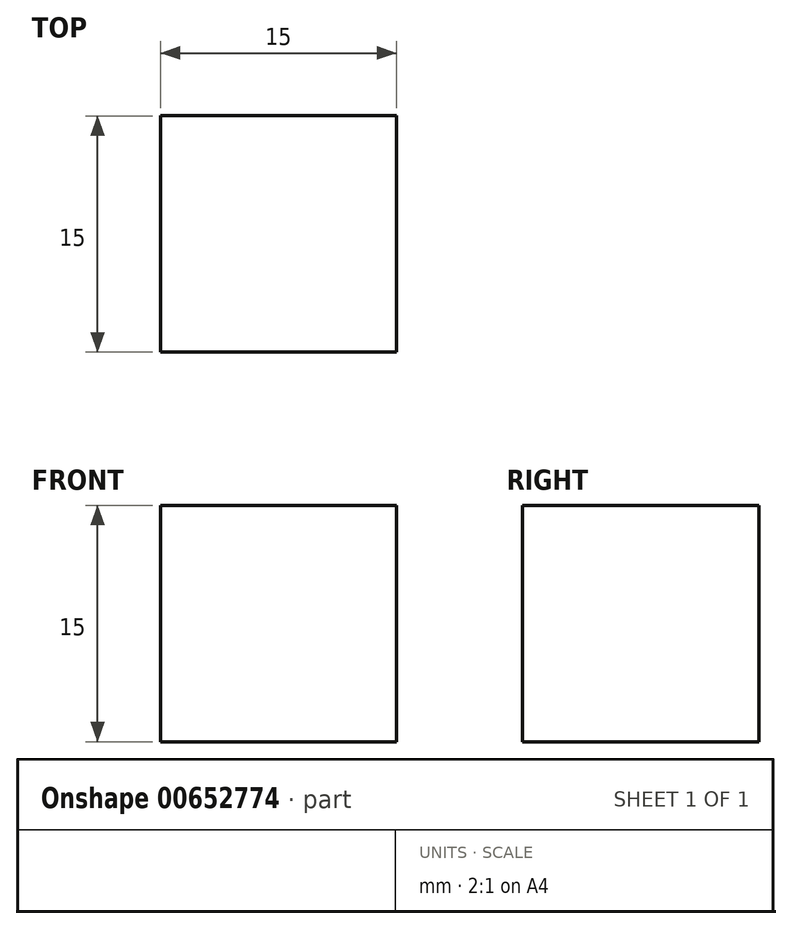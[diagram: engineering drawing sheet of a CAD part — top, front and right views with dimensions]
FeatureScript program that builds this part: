
annotation { "Feature Type Name" : "Feature", "Feature Type Description" : "" }
export const myFeature = defineFeature(function(context is Context, id is Id, definition is map)
    precondition{}
    {
        {
            var Q0;
            Q0=qCreatedBy(makeId("Top.planeOp"),FACE);
            var sketch = newSketch(context, id + "F0", { "sketchPlane" : qUnion([Q0])});
            skLineSegment(sketch, "E0.bottom", {"start": v(-45.45, -25.36) * mm, "end": v(-60.45, -25.36) * mm});
            skLineSegment(sketch, "E0.top", {"start": v(-45.45, -10.36) * mm, "end": v(-60.45, -10.36) * mm});
            skLineSegment(sketch, "E0.left", {"start": v(-45.45, -25.36) * mm, "end": v(-45.45, -10.36) * mm});
            skLineSegment(sketch, "E0.right", {"start": v(-60.45, -25.36) * mm, "end": v(-60.45, -10.36) * mm});
            skPoint(sketch, "E0.middle", {"position": v(-52.95, -17.86) * mm});
            skSolve(sketch);
        }
        {
            var Q0;
            Q0=makeQuery(id+"F0.imprint","IMPRINT",FACE,{"disambiguationData":[TD([[makeQuery(id+"F0.imprint","IMPRINT",EDGE,{"derivedFrom":sQuery(id+"F0.wireOp",EDGE,"E0.bottom")}),-1.0]])]});
            extrude(context, id + "F1", {"entities" : qUnion([Q0]), "depth" : 15 * mm, "offsetDistance" : 25 * mm});
        }
    });
